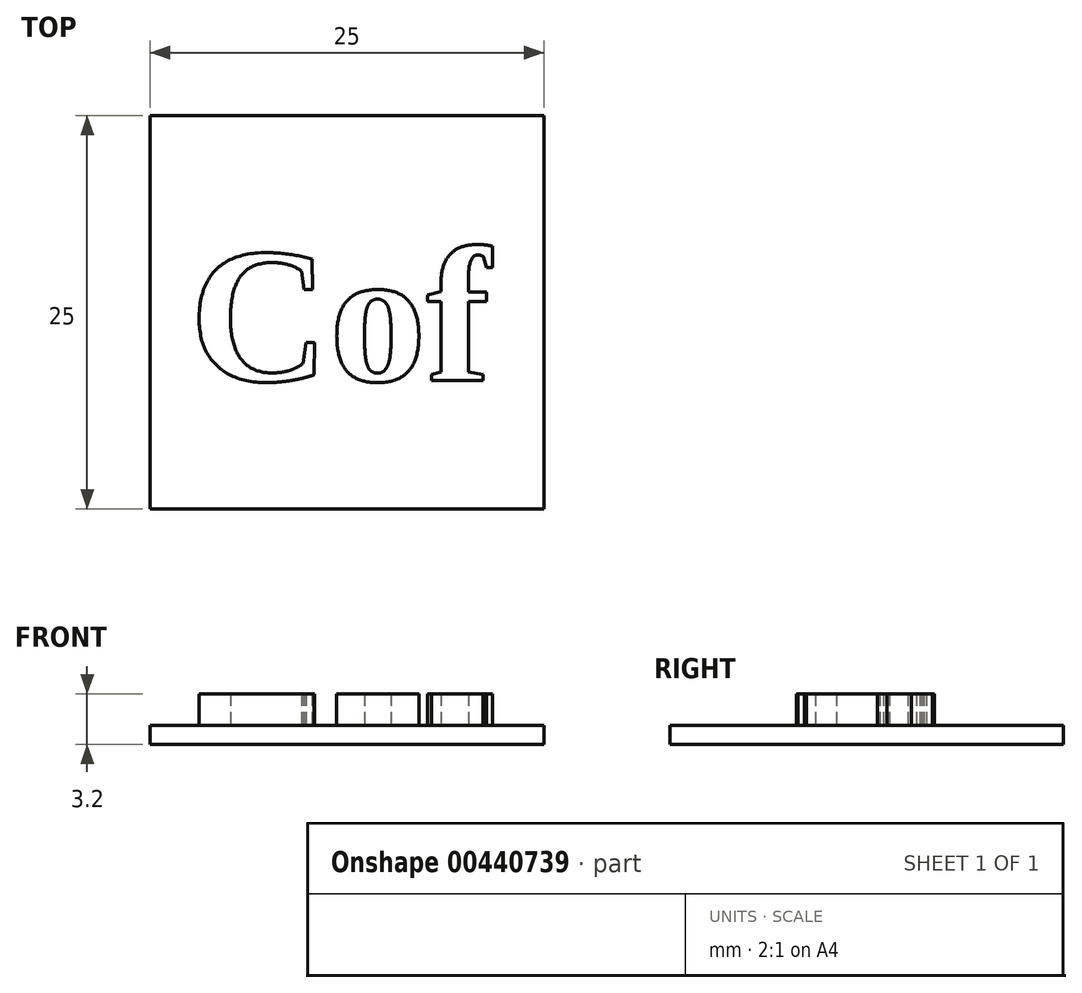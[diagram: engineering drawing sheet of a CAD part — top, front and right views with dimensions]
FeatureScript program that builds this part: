
annotation { "Feature Type Name" : "Feature", "Feature Type Description" : "" }
export const myFeature = defineFeature(function(context is Context, id is Id, definition is map)
    precondition{}
    {
        {
            var Q0;
            Q0=qCreatedBy(makeId("Top.planeOp"),FACE);
            var sketch = newSketch(context, id + "F0", { "sketchPlane" : qUnion([Q0])});
            skLineSegment(sketch, "E0.bottom", {"start": v(12.5, 12.5) * mm, "end": v(-12.5, 12.5) * mm});
            skLineSegment(sketch, "E0.top", {"start": v(12.5, -12.5) * mm, "end": v(-12.5, -12.5) * mm});
            skLineSegment(sketch, "E0.left", {"start": v(12.5, 12.5) * mm, "end": v(12.5, -12.5) * mm});
            skLineSegment(sketch, "E0.right", {"start": v(-12.5, 12.5) * mm, "end": v(-12.5, -12.5) * mm});
            skPoint(sketch, "E0.middle", {"position": v(0, 0) * mm});
            skSolve(sketch);
        }
        {
            var Q0;
            Q0=makeQuery(id+"F0.imprint","IMPRINT",FACE,{"disambiguationData":[TD([[makeQuery(id+"F0.imprint","IMPRINT",EDGE,{"derivedFrom":sQuery(id+"F0.wireOp",EDGE,"E0.bottom")}),1.0]])]});
            extrude(context, id + "F1", {"entities" : qUnion([Q0]), "depth" : 1.2 * mm});
        }
        {
            var Q0;
            Q0=makeQuery(id+"F1.opExtrude","CAP_FACE",FACE,{"disambiguationData":[OSD([sQuery(id+"F0.wireOp",EDGE,"E0.bottom"),sQuery(id+"F0.wireOp",EDGE,"E0.top"),sQuery(id+"F0.wireOp",EDGE,"E0.left"),sQuery(id+"F0.wireOp",EDGE,"E0.right")])],"isStart":false});
            var sketch = newSketch(context, id + "F2", { "sketchPlane" : qUnion([Q0])});
            skText(sketch, "E1", { "text": "Cof", "fontName": "Tinos-Bold.ttf"});
            const initialGuessF2  = {"E1": [-0.01, -0.00435, 1, 0, 0.00885]};
            skSetInitialGuess(sketch, initialGuessF2);
            skSolve(sketch);
        }
        {
            var Q0;
            Q0 = qSketchRegion(id + "F2", true);
            extrude(context, id + "F3", {"entities" : qUnion([Q0]), "operationType" : NewBodyOperationType.ADD, "depth" : 2 * mm});
        }
    });
